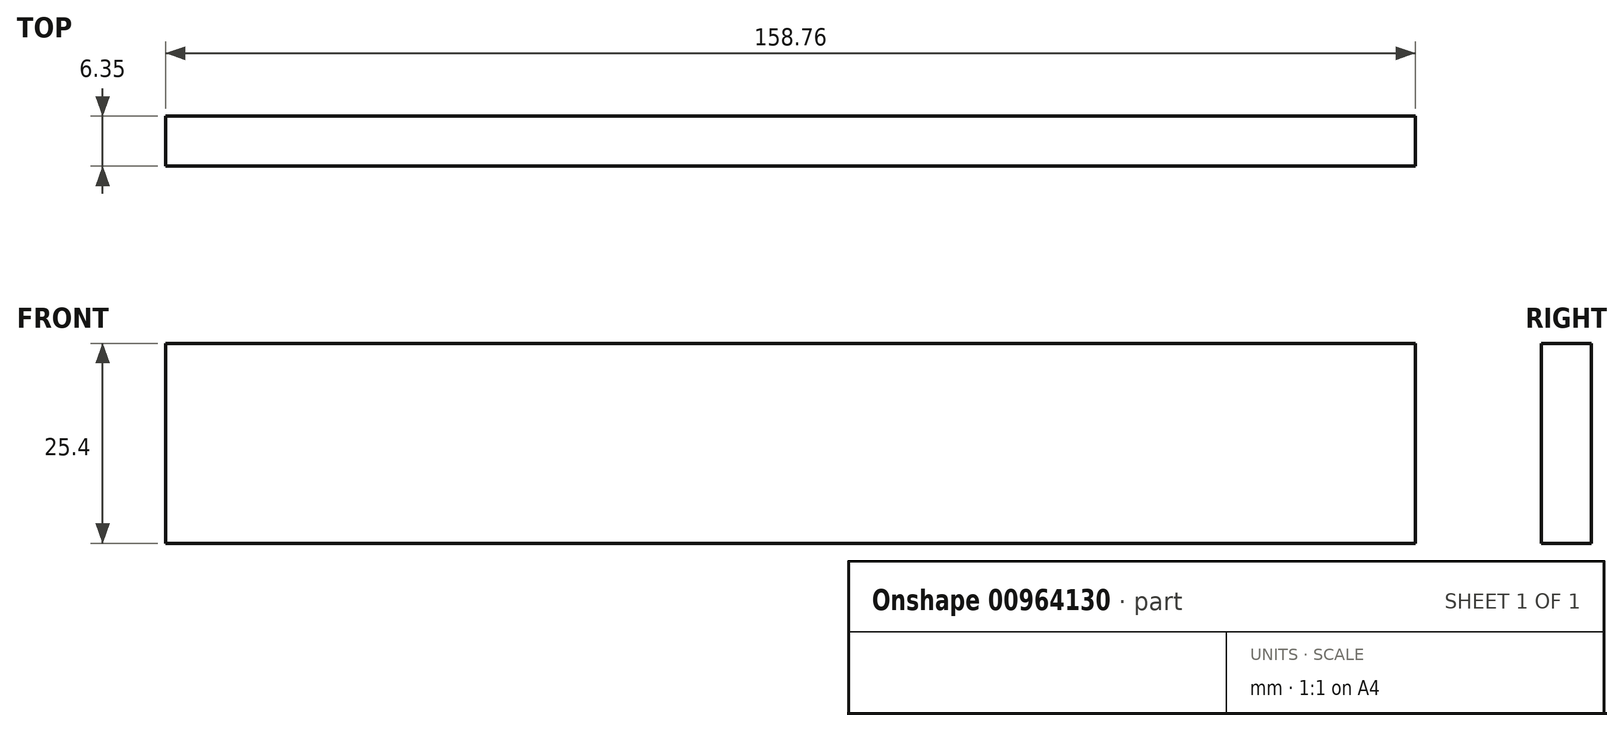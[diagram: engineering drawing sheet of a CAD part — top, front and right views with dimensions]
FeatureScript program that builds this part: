
annotation { "Feature Type Name" : "Feature", "Feature Type Description" : "" }
export const myFeature = defineFeature(function(context is Context, id is Id, definition is map)
    precondition{}
    {
        {
            var Q0;
            Q0=qCreatedBy(makeId("Front.planeOp"),FACE);
            var sketch = newSketch(context, id + "F0", { "sketchPlane" : qUnion([Q0])});
            skLineSegment(sketch, "E0.bottom", {"start": v(-79.38, 12.7) * mm, "end": v(79.38, 12.7) * mm});
            skLineSegment(sketch, "E0.top", {"start": v(-79.38, -12.7) * mm, "end": v(79.38, -12.7) * mm});
            skLineSegment(sketch, "E0.left", {"start": v(-79.38, 12.7) * mm, "end": v(-79.38, -12.7) * mm});
            skLineSegment(sketch, "E0.right", {"start": v(79.38, 12.7) * mm, "end": v(79.38, -12.7) * mm});
            skLineSegment(sketch, "E1", {"start": v(79.37, 12.7) * mm, "end": v(-79.38, -12.7) * mm, "construction": true});
            skLineSegment(sketch, "E2", {"start": v(-79.38, 12.7) * mm, "end": v(79.37, -12.7) * mm, "construction": true});
            skPoint(sketch, "E3", {"position": v(0, 0) * mm});
            skSolve(sketch);
        }
        {
            var Q0;
            Q0=makeQuery(id+"F0.imprint","IMPRINT",FACE,{"disambiguationData":[TD([[makeQuery(id+"F0.imprint","IMPRINT",EDGE,{"derivedFrom":sQuery(id+"F0.wireOp",EDGE,"E0.bottom")}),-1.0]])]});
            extrude(context, id + "F1", {"entities" : qUnion([Q0]), "depth" : 6.35 * mm, "offsetDistance" : 25.4 * mm});
        }
    });
